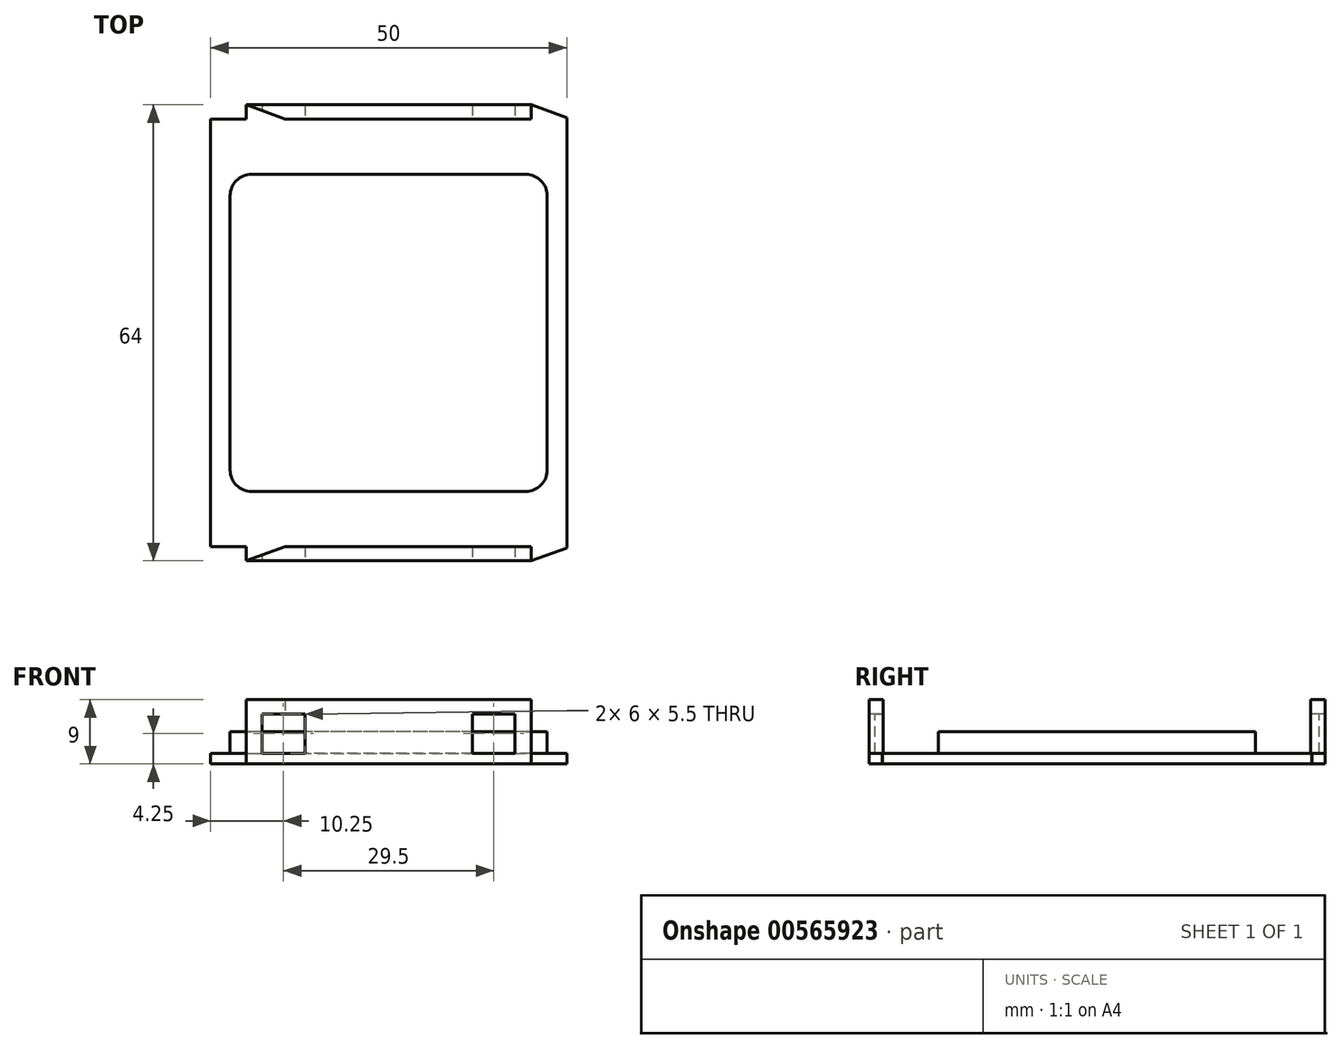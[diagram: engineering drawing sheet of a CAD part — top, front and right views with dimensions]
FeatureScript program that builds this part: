
annotation { "Feature Type Name" : "Feature", "Feature Type Description" : "" }
export const myFeature = defineFeature(function(context is Context, id is Id, definition is map)
    precondition{}
    {
        {
            var Q0;
            Q0=qCreatedBy(makeId("Top.planeOp"),FACE);
            var sketch = newSketch(context, id + "F0", { "sketchPlane" : qUnion([Q0])});
            skLineSegment(sketch, "E0.bottom", {"start": v(25, -30) * mm, "end": v(-25, -30) * mm});
            skLineSegment(sketch, "E0.top", {"start": v(25, 30) * mm, "end": v(-25, 30) * mm});
            skLineSegment(sketch, "E0.left", {"start": v(25, -30) * mm, "end": v(25, 30) * mm});
            skLineSegment(sketch, "E0.right", {"start": v(-25, -30) * mm, "end": v(-25, 30) * mm});
            skPoint(sketch, "E0.middle", {"position": v(0, 0) * mm});
            skSolve(sketch);
        }
        {
            var Q0;
            Q0=makeQuery(id+"F0.imprint","IMPRINT",FACE,{"disambiguationData":[TD([[makeQuery(id+"F0.imprint","IMPRINT",EDGE,{"derivedFrom":sQuery(id+"F0.wireOp",EDGE,"E0.bottom")}),-1.0]])]});
            extrude(context, id + "F1", {"entities" : qUnion([Q0]), "depth" : 1.5 * mm, "offsetDistance" : 25 * mm});
        }
        {
            var Q0;
            Q0=qCreatedBy(makeId("Top.planeOp"),FACE);
            var sketch = newSketch(context, id + "F2", { "sketchPlane" : qUnion([Q0])});
            skLineSegment(sketch, "E1.bottom", {"start": v(0, 32) * mm, "end": v(20, 32) * mm});
            skLineSegment(sketch, "E1.top", {"start": v(0, 30) * mm, "end": v(20, 30) * mm});
            skLineSegment(sketch, "E1.left", {"start": v(0, 32) * mm, "end": v(0, 30) * mm});
            skLineSegment(sketch, "E1.right", {"start": v(20, 32) * mm, "end": v(20, 30) * mm});
            skLineSegment(sketch, "E2.MirrorCS", {"start": v(-20, 32) * mm, "end": v(-20, 30) * mm});
            skLineSegment(sketch, "E3.MirrorCS", {"start": v(0, 32) * mm, "end": v(-20, 32) * mm});
            skLineSegment(sketch, "E4.MirrorCS", {"start": v(0, 30) * mm, "end": v(-20, 30) * mm});
            skLineSegment(sketch, "E5.MirrorCS", {"start": v(0, -32) * mm, "end": v(0, -30) * mm});
            skLineSegment(sketch, "E6.MirrorCS", {"start": v(-20, -32) * mm, "end": v(-20, -30) * mm});
            skLineSegment(sketch, "E7.MirrorCS", {"start": v(20, -32) * mm, "end": v(20, -30) * mm});
            skLineSegment(sketch, "E8.MirrorCS", {"start": v(0, -30) * mm, "end": v(-20, -30) * mm});
            skLineSegment(sketch, "E9.MirrorCS", {"start": v(0, -32) * mm, "end": v(-20, -32) * mm});
            skLineSegment(sketch, "E10.MirrorCS", {"start": v(0, -32) * mm, "end": v(20, -32) * mm});
            skLineSegment(sketch, "E11.MirrorCS", {"start": v(0, -30) * mm, "end": v(20, -30) * mm});
            skSolve(sketch);
        }
        {
            var Q0;
            Q0 = qSketchRegion(id + "F2", true);
            extrude(context, id + "F3", {"entities" : qUnion([Q0]), "operationType" : NewBodyOperationType.ADD, "depth" : 9 * mm, "offsetDistance" : 25 * mm});
        }
        {
            var Q0;
            Q0=qCreatedBy(makeId("Front.planeOp"),FACE);
            var sketch = newSketch(context, id + "F4", { "sketchPlane" : qUnion([Q0])});
            skLineSegment(sketch, "E12.bottom", {"start": v(-17.75, 7) * mm, "end": v(-11.75, 7) * mm});
            skLineSegment(sketch, "E12.top", {"start": v(-17.75, 1.5) * mm, "end": v(-11.75, 1.5) * mm});
            skLineSegment(sketch, "E12.left", {"start": v(-17.75, 7) * mm, "end": v(-17.75, 1.5) * mm});
            skLineSegment(sketch, "E12.right", {"start": v(-11.75, 7) * mm, "end": v(-11.75, 1.5) * mm});
            skLineSegment(sketch, "E13.MirrorCS", {"start": v(17.75, 7) * mm, "end": v(11.75, 7) * mm});
            skLineSegment(sketch, "E14.MirrorCS", {"start": v(17.75, 7) * mm, "end": v(17.75, 1.5) * mm});
            skLineSegment(sketch, "E15.MirrorCS", {"start": v(17.75, 1.5) * mm, "end": v(11.75, 1.5) * mm});
            skLineSegment(sketch, "E16.MirrorCS", {"start": v(11.75, 7) * mm, "end": v(11.75, 1.5) * mm});
            skSolve(sketch);
        }
        {
            var Q0;
            Q0 = qSketchRegion(id + "F4", true);
            extrude(context, id + "F5", {"entities" : qUnion([Q0]), "operationType" : NewBodyOperationType.REMOVE, "endBound" : BoundingType.SYMMETRIC, "oppositeDirection" : true, "depth" : 64 * mm, "offsetDistance" : 25 * mm});
        }
        {
            var Q0;
            Q0=qCreatedBy(makeId("Top.planeOp"),FACE);
            var sketch = newSketch(context, id + "F6", { "sketchPlane" : qUnion([Q0])});
            skLineSegment(sketch, "E17.bottom", {"start": v(22.25, -22.25) * mm, "end": v(-22.25, -22.25) * mm});
            skLineSegment(sketch, "E17.top", {"start": v(22.25, 22.25) * mm, "end": v(-22.25, 22.25) * mm});
            skLineSegment(sketch, "E17.left", {"start": v(22.25, -22.25) * mm, "end": v(22.25, 22.25) * mm});
            skLineSegment(sketch, "E17.right", {"start": v(-22.25, -22.25) * mm, "end": v(-22.25, 22.25) * mm});
            skPoint(sketch, "E17.middle", {"position": v(0, 0) * mm});
            skSolve(sketch);
        }
        {
            var Q0;
            Q0 = qSketchRegion(id + "F6", true);
            extrude(context, id + "F7", {"entities" : qUnion([Q0]), "operationType" : NewBodyOperationType.ADD, "depth" : 4.5 * mm, "offsetDistance" : 25 * mm});
        }
        {
            var Q0;
            Q0=makeQuery(id+"F7.opExtrude","SWEPT_EDGE",EDGE,{"disambiguationData":[OSD([sQuery(id+"F6.wireOp",EDGE,"E17.bottom"),sQuery(id+"F6.wireOp",EDGE,"E17.left")])]});
            var Q1;
            Q1=makeQuery(id+"F7.opExtrude","SWEPT_EDGE",EDGE,{"disambiguationData":[OSD([sQuery(id+"F6.wireOp",EDGE,"E17.bottom"),sQuery(id+"F6.wireOp",EDGE,"E17.right")])]});
            var Q2;
            Q2=makeQuery(id+"F7.opExtrude","SWEPT_EDGE",EDGE,{"disambiguationData":[OSD([sQuery(id+"F6.wireOp",EDGE,"E17.top"),sQuery(id+"F6.wireOp",EDGE,"E17.right")])]});
            var Q3;
            Q3=makeQuery(id+"F7.opExtrude","SWEPT_EDGE",EDGE,{"disambiguationData":[OSD([sQuery(id+"F6.wireOp",EDGE,"E17.top"),sQuery(id+"F6.wireOp",EDGE,"E17.left")])]});
            fillet(context, id + "F8", {"entities" : qUnion([Q0, Q1, Q2, Q3]), "radius" : 3 * mm, "tangentPropagation" : true, "allowEdgeOverflow" : false});
        }
        {
            var Q0;
            {var subQ0=sQuery(id+"F2.wireOp",EDGE,"E1.right");Q0=makeQuery(id+"F3.boolean.opBoolean","SPLIT",EDGE,{"disambiguationData":[topologyDisambiguationEdgeConnected([makeQuery(id+"F1.opExtrude","SWEPT_FACE",FACE,{"disambiguationData":[OSD([sQuery(id+"F0.wireOp",EDGE,"E0.top")])]})])],"derivedFrom":makeQuery(id+"F3.opExtrude","SWEPT_EDGE",EDGE,{"disambiguationData":[OSD([sQuery(id+"F2.wireOp",EDGE,"E1.top"),subQ0])]})});}
            var Q1;
            {var subQ0=sQuery(id+"F2.wireOp",EDGE,"E6.MirrorCS");Q1=makeQuery(id+"F3.boolean.opBoolean","SPLIT",EDGE,{"disambiguationData":[topologyDisambiguationEdgeConnected([makeQuery(id+"F1.opExtrude","SWEPT_FACE",FACE,{"disambiguationData":[OSD([sQuery(id+"F0.wireOp",EDGE,"E0.bottom")])]})])],"derivedFrom":makeQuery(id+"F3.opExtrude","SWEPT_EDGE",EDGE,{"disambiguationData":[OSD([subQ0,sQuery(id+"F2.wireOp",EDGE,"E8.MirrorCS")])]})});}
            chamfer(context, id + "F9", {"entities" : qUnion([Q0, Q1]), "chamferType" : ChamferType.OFFSET_ANGLE, "width" : 2 * mm, "oppositeDirection" : false, "angle" : 70 * degree, "tangentPropagation" : true});
        }
        {
            var Q0;
            {var subQ0=sQuery(id+"F2.wireOp",EDGE,"E2.MirrorCS");Q0=makeQuery(id+"F3.boolean.opBoolean","SPLIT",EDGE,{"disambiguationData":[topologyDisambiguationEdgeConnected([makeQuery(id+"F1.opExtrude","SWEPT_FACE",FACE,{"disambiguationData":[OSD([sQuery(id+"F0.wireOp",EDGE,"E0.top")])]})])],"derivedFrom":makeQuery(id+"F3.opExtrude","SWEPT_EDGE",EDGE,{"disambiguationData":[OSD([subQ0,sQuery(id+"F2.wireOp",EDGE,"E4.MirrorCS")])]})});}
            var Q1;
            {var subQ0=sQuery(id+"F2.wireOp",EDGE,"E7.MirrorCS");Q1=makeQuery(id+"F3.boolean.opBoolean","SPLIT",EDGE,{"disambiguationData":[topologyDisambiguationEdgeConnected([makeQuery(id+"F1.opExtrude","SWEPT_FACE",FACE,{"disambiguationData":[OSD([sQuery(id+"F0.wireOp",EDGE,"E0.bottom")])]})])],"derivedFrom":makeQuery(id+"F3.opExtrude","SWEPT_EDGE",EDGE,{"disambiguationData":[OSD([subQ0,sQuery(id+"F2.wireOp",EDGE,"E11.MirrorCS")])]})});}
            chamfer(context, id + "F10", {"entities" : qUnion([Q0, Q1]), "chamferType" : ChamferType.OFFSET_ANGLE, "width" : 2 * mm, "oppositeDirection" : true, "angle" : 70 * degree, "tangentPropagation" : true});
        }
    });
